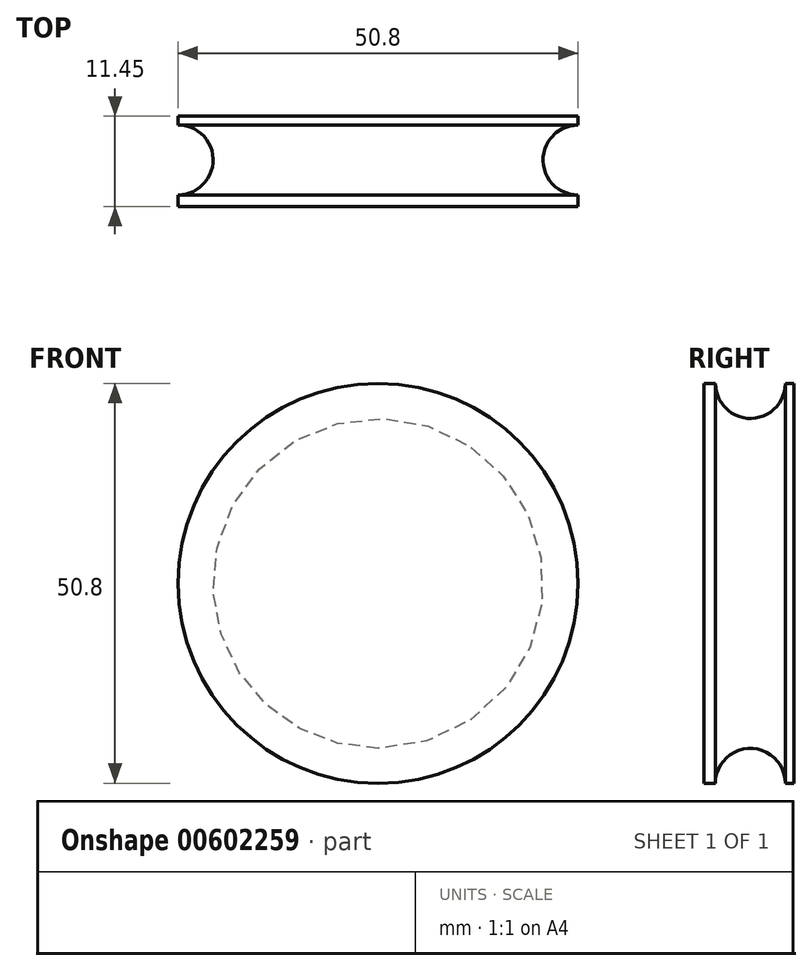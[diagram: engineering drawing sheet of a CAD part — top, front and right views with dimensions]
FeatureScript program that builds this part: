
annotation { "Feature Type Name" : "Feature", "Feature Type Description" : "" }
export const myFeature = defineFeature(function(context is Context, id is Id, definition is map)
    precondition{}
    {
        {
            var Q0;
            Q0=qCreatedBy(makeId("Top.planeOp"),FACE);
            var sketch = newSketch(context, id + "F0", { "sketchPlane" : qUnion([Q0])});
            skLineSegment(sketch, "E0", {"start": v(0, 5.56) * mm, "end": v(0, -5.87) * mm});
            skLineSegment(sketch, "E1", {"start": v(1.6, -5.89) * mm, "end": v(1.6, 5.56) * mm});
            skLineSegment(sketch, "E2", {"start": v(1.6, 5.56) * mm, "end": v(0, 5.56) * mm});
            skLineSegment(sketch, "E3", {"start": v(0, -5.87) * mm, "end": v(1.6, -5.89) * mm});
            skLineSegment(sketch, "E4", {"start": v(1.6, -5.89) * mm, "end": v(27, -5.89) * mm});
            skLineSegment(sketch, "E5", {"start": v(1.6, 5.56) * mm, "end": v(27, 5.56) * mm});
            skCircle(sketch, "E6", {"center": v(27, 0) * mm, "radius": 4.45 * mm});
            skLineSegment(sketch, "E7", {"start": v(27, -5.89) * mm, "end": v(27, -4.45) * mm});
            skLineSegment(sketch, "E8", {"start": v(27, 5.56) * mm, "end": v(27, 4.45) * mm});
            skSolve(sketch);
        }
        {
            var Q0;
            Q0=makeQuery(id+"F0.imprint","IMPRINT",FACE,{"disambiguationData":[TD([[makeQuery(id+"F0.imprint","IMPRINT",EDGE,{"derivedFrom":sQuery(id+"F0.wireOp",EDGE,"E1")}),-1.0]])]});
            var Q1;
            Q1=sQuery(id+"F0.wireOp",EDGE,"E1");
            revolve(context, id + "F1", {"entities" : qUnion([Q0]), "axis" : qUnion([Q1]), "revolveType" : RevolveType.FULL});
        }
        {
            var Q0;
            Q0=qCreatedBy(makeId("Top.planeOp"),FACE);
            var sketch = newSketch(context, id + "F2", { "sketchPlane" : qUnion([Q0])});
            skLineSegment(sketch, "E9", {"start": v(27, -4.45) * mm, "end": v(-23.8, -4.45) * mm});
            skLineSegment(sketch, "E10", {"start": v(27, 4.45) * mm, "end": v(-23.8, 4.45) * mm});
            skArc(sketch, "E11", {"start": v(27, 4.45) * mm, "mid": v(22.56, 0) * mm, "end": v(27, -4.45) * mm});
            skArc(sketch, "E12", {"start": v(-23.8, -4.45) * mm, "mid": v(-19.35, 0) * mm, "end": v(-23.8, 4.45) * mm});
            skLineSegment(sketch, "E13", {"start": v(27, -4.45) * mm, "end": v(-23.8, -4.45) * mm, "construction": true});
            skLineSegment(sketch, "E14", {"start": v(27, 4.45) * mm, "end": v(-23.8, 4.45) * mm, "construction": true});
            skArc(sketch, "E15", {"start": v(27, 4.45) * mm, "mid": v(22.56, 0) * mm, "end": v(27, -4.45) * mm, "construction": true});
            skArc(sketch, "E16", {"start": v(-23.8, -4.45) * mm, "mid": v(-19.35, 0) * mm, "end": v(-23.8, 4.45) * mm, "construction": true});
            skPoint(sketch, "E17.0", {"position": v(0, 0) * mm});
            skSolve(sketch);
        }
        {
            var Q0;
            Q0=qCreatedBy(makeId("Top.planeOp"),FACE);
            cPlane(context, id + "F3", {"entities" : qUnion([Q0]), "cplaneType" : CPlaneType.OFFSET, "offset" : 20.7 * mm, "width" : 152.4 * mm, "height" : 152.4 * mm});
        }
        {
            var Q0;
            Q0=qCreatedBy(id+"F3.planeOp",FACE);
            var sketch = newSketch(context, id + "F4", { "sketchPlane" : qUnion([Q0])});
            skPoint(sketch, "E18.0", {"position": v(0, 0) * mm});
            skLineSegment(sketch, "E19", {"start": v(-9.27, 0) * mm, "end": v(14.59, 0) * mm, "construction": true});
            skCircle(sketch, "E20", {"center": v(0, 0) * mm, "radius": 1.27 * mm});
            skSolve(sketch);
        }
        {
            var Q0;
            Q0=sQuery(id+"F4.wireOp",EDGE,"E20");
            extrude(context, id + "F5", {"bodyType" : ToolBodyType.SURFACE, "surfaceEntities" : qUnion([Q0]), "depth" : 1.52 * mm, "offsetDistance" : 25.4 * mm});
        }
    });
